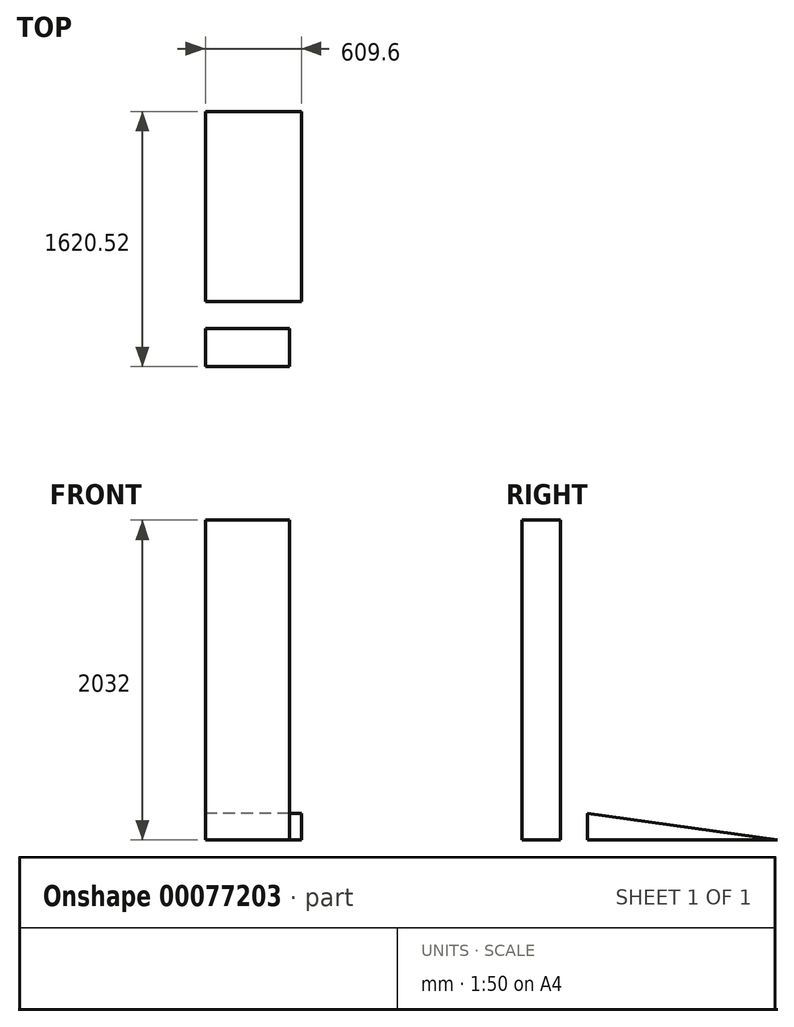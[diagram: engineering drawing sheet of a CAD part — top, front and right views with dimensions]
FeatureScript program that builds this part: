
annotation { "Feature Type Name" : "Feature", "Feature Type Description" : "" }
export const myFeature = defineFeature(function(context is Context, id is Id, definition is map)
    precondition{}
    {
        {
            var Q0;
            Q0=qCreatedBy(makeId("Right.planeOp"),FACE);
            var sketch = newSketch(context, id + "F0", { "sketchPlane" : qUnion([Q0])});
            skLineSegment(sketch, "E0", {"start": v(170.36, 0) * mm, "end": v(1377.7, 0) * mm});
            skLineSegment(sketch, "E1", {"start": v(1377.7, 0) * mm, "end": v(170.36, 169.68) * mm});
            skLineSegment(sketch, "E2", {"start": v(170.36, 169.68) * mm, "end": v(170.36, 0) * mm});
            skSolve(sketch);
        }
        {
            var Q0;
            Q0=makeQuery(id+"F0.imprint","IMPRINT",FACE,{"disambiguationData":[TD([[makeQuery(id+"F0.imprint","IMPRINT",EDGE,{"derivedFrom":sQuery(id+"F0.wireOp",EDGE,"E0")}),1.0]])]});
            extrude(context, id + "F1", {"entities" : qUnion([Q0]), "depth" : 609.6 * mm});
        }
        {
            var Q0;
            Q0=qCreatedBy(makeId("Right.planeOp"),FACE);
            var sketch = newSketch(context, id + "F2", { "sketchPlane" : qUnion([Q0])});
            skLineSegment(sketch, "E3", {"start": v(0, 0) * mm, "end": v(0, 2032) * mm});
            skLineSegment(sketch, "E4", {"start": v(0, 2032) * mm, "end": v(-242.82, 2032) * mm});
            skLineSegment(sketch, "E5", {"start": v(-242.82, 2032) * mm, "end": v(-242.82, 0) * mm});
            skLineSegment(sketch, "E6", {"start": v(-242.82, 0) * mm, "end": v(0, 0) * mm});
            skSolve(sketch);
        }
        {
            var Q0;
            Q0=makeQuery(id+"F2.imprint","IMPRINT",FACE,{"disambiguationData":[TD([[makeQuery(id+"F2.imprint","IMPRINT",EDGE,{"derivedFrom":sQuery(id+"F2.wireOp",EDGE,"E3")}),1.0]])]});
            extrude(context, id + "F3", {"entities" : qUnion([Q0]), "depth" : 533.4 * mm});
        }
    });
